# Revit family: ACO TD-200 Neutral channel
name_source: partatom
category: Plumbing Fixtures
units: mm (PartAtom-declared; Revit-internal decimal feet)

## family parameters
Always vertical = Yes
Cut with Voids When Loaded = No
OmniClass Number = 23.70.50.24
OmniClass Title = Rainwater Removal
Part Type = Normal
Room Calculation Point = No
Round Connector Dimension = Use Diameter
Shared = No
Work Plane-Based = No

## types (5) — shared parameters
Description = ACO TD200 Neutral channel
IfcDescription = ACO TD200 Neutral channel
IfcExportAs = IfcWasteTerminalType
IfcExportType = USERDEFINED
LOD = LOD 300
Manufacturer = ACO
Model = TD200 Neutral channel
Telephone = 1300 765 226
URL = https://www.acoinfrastructure.com.au
Uniclass 2015 Code = Ss_50_30_02
Uniclass 2015 Title = Rainwater drainage systems
content_date_changed_C_ANZRS = 20-07-2021
content_version_C_ANZRS = 1.0
info_commercial_C_ANZRS = https://www.acoinfrastructure.com.au
info_technical_C_ANZRS = https://www.acoinfrastructure.com.au
installation_manual = https://www.acoinfrastructure.com.au
instructions_for_use = https://www.acoinfrastructure.com.au
intended_use_C_ANZRS = Drainage systems
lookup_table_name = Neutral channel_TD200
material_01_C_ANZRS = Polymer Concrete
material_C_ANZRS = Iron, cast
region_index = 1

## per-type parameters (varying)
| type | type_index |
| TD2-00 Neutral channel | 1 |
| TD2-020 Neutral channel | 3 |
| TD2-010 Neutral channel | 2 |
| TD2-030 Neutral channel | 4 |
| TD2-040 Neutral channel | 5 |

## geometry (parser evidence)
native form markers: Sweep x8
no freeform markers — native parametric forms only
